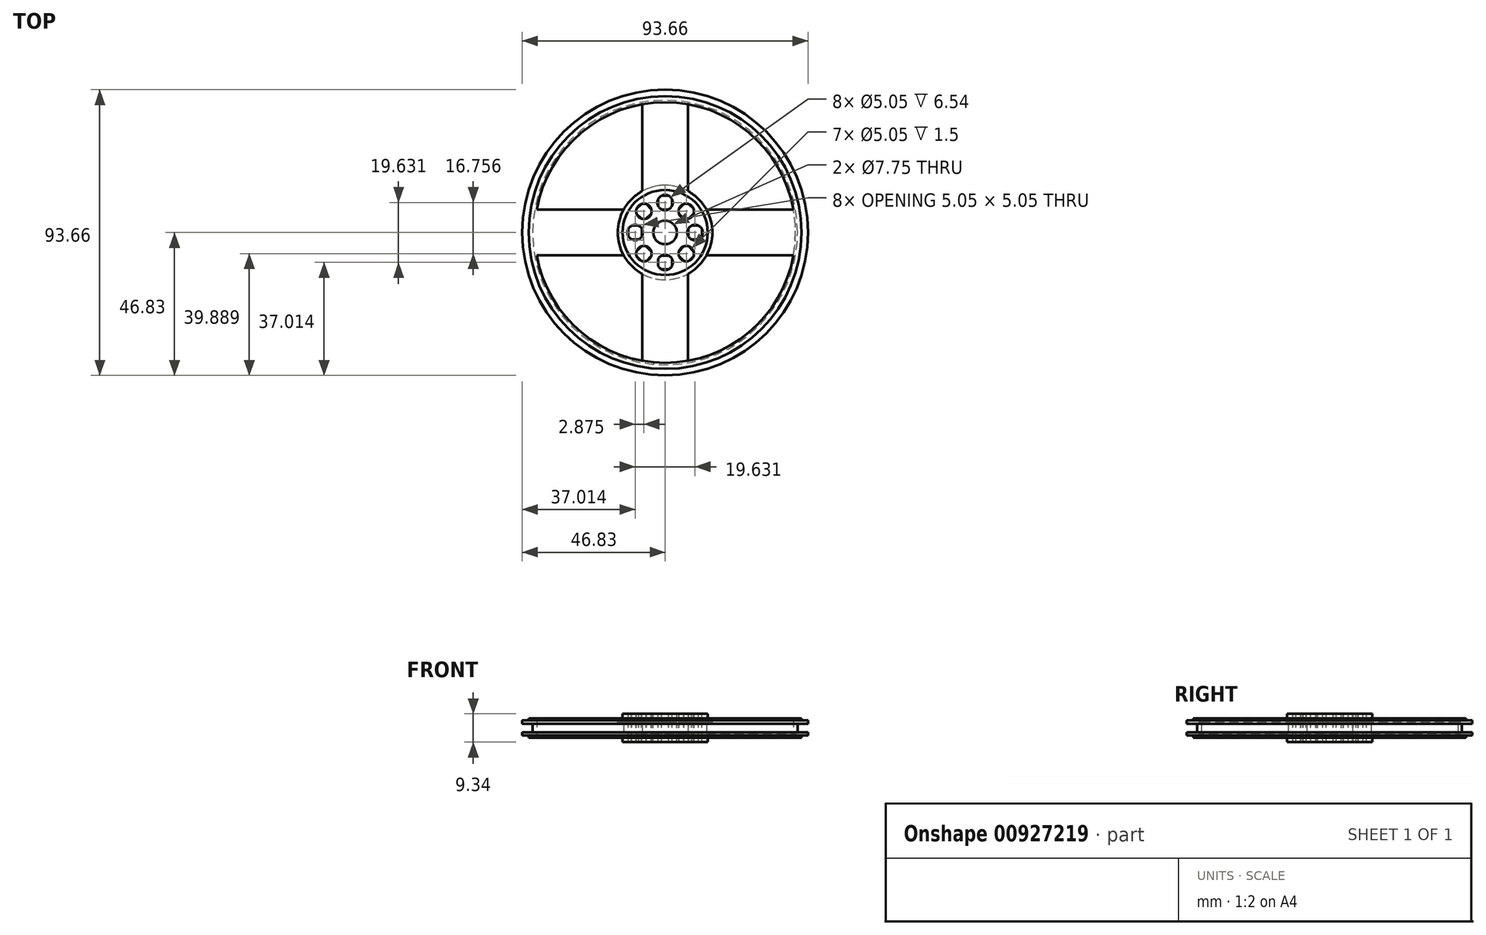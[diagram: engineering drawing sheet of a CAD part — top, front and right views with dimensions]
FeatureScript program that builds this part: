
annotation { "Feature Type Name" : "Feature", "Feature Type Description" : "" }
export const myFeature = defineFeature(function(context is Context, id is Id, definition is map)
    precondition{}
    {
        {
            var Q0;
            Q0=qCreatedBy(makeId("Top.planeOp"),FACE);
            var sketch = newSketch(context, id + "F0", { "sketchPlane" : qUnion([Q0])});
            skCircle(sketch, "E0", {"center": v(0, 0) * mm, "radius": 43.4 * mm});
            skSolve(sketch);
        }
        {
            var Q0;
            Q0 = qSketchRegion(id + "F0", true);
            extrude(context, id + "F1", {"entities" : qUnion([Q0]), "depth" : 2.82 * mm, "offsetDistance" : 25 * mm});
        }
        {
            var Q0;
            Q0=makeQuery(id+"F1.opExtrude","CAP_FACE",FACE,{"disambiguationData":[OSD([sQuery(id+"F0.wireOp",EDGE,"E0")])],"isStart":false});
            var sketch = newSketch(context, id + "F2", { "sketchPlane" : qUnion([Q0])});
            skCircle(sketch, "E1", {"center": v(0, 0) * mm, "radius": 46.83 * mm});
            skSolve(sketch);
        }
        {
            var Q0;
            Q0 = qSketchRegion(id + "F2", true);
            extrude(context, id + "F3", {"entities" : qUnion([Q0]), "operationType" : NewBodyOperationType.ADD, "depth" : 1.06 * mm, "offsetDistance" : 25 * mm});
        }
        {
            var Q0;
            Q0=makeQuery(id+"F1.opExtrude","CAP_FACE",FACE,{"disambiguationData":[OSD([sQuery(id+"F0.wireOp",EDGE,"E0")])],"isStart":true});
            var sketch = newSketch(context, id + "F4", { "sketchPlane" : qUnion([Q0])});
            skCircle(sketch, "E2.0", {"center": v(0, 0) * mm, "radius": 46.83 * mm});
            skSolve(sketch);
        }
        {
            var Q0;
            Q0 = qSketchRegion(id + "F4", true);
            extrude(context, id + "F5", {"entities" : qUnion([Q0]), "operationType" : NewBodyOperationType.ADD, "depth" : 1.06 * mm, "offsetDistance" : 25 * mm});
        }
        {
            var Q0;
            Q0=makeQuery(id+"F5.opExtrude","CAP_FACE",FACE,{"disambiguationData":[OSD([sQuery(id+"F4.wireOp",EDGE,"E2.0")])],"isStart":false});
            var sketch = newSketch(context, id + "F6", { "sketchPlane" : qUnion([Q0])});
            skCircle(sketch, "E3", {"center": v(0, 0) * mm, "radius": 44.73 * mm});
            skSolve(sketch);
        }
        {
            var Q0;
            Q0 = qSketchRegion(id + "F6", true);
            extrude(context, id + "F7", {"entities" : qUnion([Q0]), "operationType" : NewBodyOperationType.ADD, "depth" : .7 * mm, "offsetDistance" : 25 * mm});
        }
        {
            var Q0;
            Q0=makeQuery(id+"F3.opExtrude","CAP_FACE",FACE,{"disambiguationData":[OSD([sQuery(id+"F2.wireOp",EDGE,"E1")])],"isStart":false});
            var sketch = newSketch(context, id + "F8", { "sketchPlane" : qUnion([Q0])});
            skCircle(sketch, "E4.0", {"center": v(0, 0) * mm, "radius": 44.73 * mm});
            skSolve(sketch);
        }
        {
            var Q0;
            Q0 = qSketchRegion(id + "F8", true);
            extrude(context, id + "F9", {"entities" : qUnion([Q0]), "operationType" : NewBodyOperationType.ADD, "depth" : .7 * mm, "offsetDistance" : 25 * mm});
        }
        {
            var Q0;
            Q0=makeQuery(id+"F7.opExtrude","CAP_FACE",FACE,{"disambiguationData":[OSD([sQuery(id+"F6.wireOp",EDGE,"E3")])],"isStart":false});
            var sketch = newSketch(context, id + "F10", { "sketchPlane" : qUnion([Q0])});
            skCircle(sketch, "E5", {"center": v(0, 0) * mm, "radius": 15.5 * mm});
            skLineSegment(sketch, "E6", {"start": v(0, 0) * mm, "end": v(0, -44.73) * mm, "construction": true});
            skLineSegment(sketch, "E7", {"start": v(0, -44.73) * mm, "end": v(0, 44.73) * mm, "construction": true});
            skLineSegment(sketch, "E8", {"start": v(-44.73, 0) * mm, "end": v(44.73, 0) * mm, "construction": true});
            skLineSegment(sketch, "E9", {"start": v(-7.47, -13.58) * mm, "end": v(-7.47, -44.1) * mm});
            skLineSegment(sketch, "E10", {"start": v(7.47, -13.58) * mm, "end": v(7.47, -44.1) * mm});
            skLineSegment(sketch, "E11", {"start": v(7.47, -28.84) * mm, "end": v(0, -28.84) * mm, "construction": true});
            skLineSegment(sketch, "E12", {"start": v(0, -28.84) * mm, "end": v(-7.47, -28.84) * mm, "construction": true});
            skLineSegment(sketch, "E13.1.0", {"start": v(13.58, -7.48) * mm, "end": v(44.1, -7.48) * mm});
            skLineSegment(sketch, "E13.1.1", {"start": v(13.58, 7.47) * mm, "end": v(44.1, 7.47) * mm});
            skLineSegment(sketch, "E13.2.0", {"start": v(7.48, 13.58) * mm, "end": v(7.48, 44.1) * mm});
            skLineSegment(sketch, "E13.2.1", {"start": v(-7.47, 13.58) * mm, "end": v(-7.47, 44.1) * mm});
            skLineSegment(sketch, "E13.3.0", {"start": v(-13.58, 7.48) * mm, "end": v(-44.1, 7.48) * mm});
            skLineSegment(sketch, "E13.3.1", {"start": v(-13.58, -7.47) * mm, "end": v(-44.1, -7.47) * mm});
            skCircle(sketch, "E14", {"center": v(0, 0) * mm, "radius": 42.73 * mm});
            skSolve(sketch);
        }
        {
            var Q0;
            {var subQ0=sQuery(id+"F10.wireOp",EDGE,"E9");var subQ1=sQuery(id+"F10.wireOp",EDGE,"E5");var subQ2=makeQuery(id+"F10.imprint","INTERSECT",VERTEX,{"derivedFrom":[subQ1,subQ0]});Q0=makeQuery(id+"F10.imprint","IMPRINT",FACE,{"disambiguationData":[TD([[makeQuery(id+"F10.imprint","IMPRINT",EDGE,{"disambiguationData":[TD([[subQ2,1.0]])],"derivedFrom":subQ1}),-1.0]])]});}
            var Q1;
            {var subQ0=sQuery(id+"F10.wireOp",EDGE,"E13.2.1");var subQ1=sQuery(id+"F10.wireOp",EDGE,"E5");var subQ2=makeQuery(id+"F10.imprint","INTERSECT",VERTEX,{"derivedFrom":[subQ1,subQ0]});Q1=makeQuery(id+"F10.imprint","IMPRINT",FACE,{"disambiguationData":[TD([[makeQuery(id+"F10.imprint","IMPRINT",EDGE,{"disambiguationData":[TD([[subQ2,-1.0]])],"derivedFrom":subQ1}),-1.0]])]});}
            var Q2;
            {var subQ0=sQuery(id+"F10.wireOp",EDGE,"E13.1.1");var subQ1=sQuery(id+"F10.wireOp",EDGE,"E5");var subQ2=makeQuery(id+"F10.imprint","INTERSECT",VERTEX,{"derivedFrom":[subQ1,subQ0]});Q2=makeQuery(id+"F10.imprint","IMPRINT",FACE,{"disambiguationData":[TD([[makeQuery(id+"F10.imprint","IMPRINT",EDGE,{"disambiguationData":[TD([[subQ2,-1.0]])],"derivedFrom":subQ1}),-1.0]])]});}
            var Q3;
            {var subQ0=sQuery(id+"F10.wireOp",EDGE,"E10");var subQ1=sQuery(id+"F10.wireOp",EDGE,"E5");var subQ2=makeQuery(id+"F10.imprint","INTERSECT",VERTEX,{"derivedFrom":[subQ1,subQ0]});Q3=makeQuery(id+"F10.imprint","IMPRINT",FACE,{"disambiguationData":[TD([[makeQuery(id+"F10.imprint","IMPRINT",EDGE,{"disambiguationData":[TD([[subQ2,-1.0]])],"derivedFrom":subQ1}),-1.0]])]});}
            extrude(context, id + "F11", {"entities" : qUnion([Q0, Q1, Q2, Q3]), "operationType" : NewBodyOperationType.REMOVE, "oppositeDirection" : true, "depth" : 25 * mm, "offsetDistance" : 25 * mm});
        }
        {
            var Q0;
            {var subQ0=sQuery(id+"F10.wireOp",EDGE,"E13.3.0");Q0=makeQuery(id+"F10.imprint","IMPRINT",FACE,{"disambiguationData":[TD([[makeQuery(id+"F10.imprint","IMPRINT",EDGE,{"derivedFrom":subQ0}),1.0]])]});}
            var sketch = newSketch(context, id + "F12", { "sketchPlane" : qUnion([Q0])});
            skSolve(sketch);
        }
        {
            var Q0;
            {var subQ0=sQuery(id+"F10.wireOp",EDGE,"E13.3.0");var subQ1=sQuery(id+"F10.wireOp",EDGE,"E5");var subQ2=makeQuery(id+"F10.imprint","INTERSECT",VERTEX,{"derivedFrom":[subQ1,subQ0]});Q0=makeQuery(id+"F12.imprint","IMPRINT",FACE,{"disambiguationData":[TD([[makeQuery(id+"F12.imprint","IMPRINT",EDGE,{"derivedFrom":makeQuery(id+"F10.imprint","IMPRINT",EDGE,{"disambiguationData":[TD([[subQ2,-1.0]])],"derivedFrom":subQ1})}),-1.0]])]});}
            var Q1;
            {var subQ0=sQuery(id+"F10.wireOp",EDGE,"E9");var subQ1=sQuery(id+"F10.wireOp",EDGE,"E5");var subQ2=makeQuery(id+"F10.imprint","INTERSECT",VERTEX,{"derivedFrom":[subQ1,subQ0]});Q1=makeQuery(id+"F10.imprint","IMPRINT",FACE,{"disambiguationData":[TD([[makeQuery(id+"F10.imprint","IMPRINT",EDGE,{"disambiguationData":[TD([[subQ2,-1.0]])],"derivedFrom":subQ1}),-1.0]])]});}
            var Q2;
            {var subQ0=sQuery(id+"F10.wireOp",EDGE,"E13.1.0");var subQ1=sQuery(id+"F10.wireOp",EDGE,"E5");var subQ2=makeQuery(id+"F10.imprint","INTERSECT",VERTEX,{"derivedFrom":[subQ1,subQ0]});Q2=makeQuery(id+"F10.imprint","IMPRINT",FACE,{"disambiguationData":[TD([[makeQuery(id+"F10.imprint","IMPRINT",EDGE,{"disambiguationData":[TD([[subQ2,-1.0]])],"derivedFrom":subQ1}),-1.0]])]});}
            var Q3;
            {var subQ0=sQuery(id+"F10.wireOp",EDGE,"E13.2.0");var subQ1=sQuery(id+"F10.wireOp",EDGE,"E5");var subQ2=makeQuery(id+"F10.imprint","INTERSECT",VERTEX,{"derivedFrom":[subQ1,subQ0]});Q3=makeQuery(id+"F10.imprint","IMPRINT",FACE,{"disambiguationData":[TD([[makeQuery(id+"F10.imprint","IMPRINT",EDGE,{"disambiguationData":[TD([[subQ2,-1.0]])],"derivedFrom":subQ1}),-1.0]])]});}
            extrude(context, id + "F13", {"entities" : qUnion([Q0, Q1, Q2, Q3]), "operationType" : NewBodyOperationType.REMOVE, "oppositeDirection" : true, "depth" : 1.3 * mm, "offsetDistance" : 25 * mm});
        }
        {
            var Q0;
            Q0=makeQuery(id+"F9.opExtrude","CAP_FACE",FACE,{"disambiguationData":[OSD([sQuery(id+"F8.wireOp",EDGE,"E4.0")])],"isStart":false});
            var sketch = newSketch(context, id + "F14", { "sketchPlane" : qUnion([Q0])});
            skCircle(sketch, "E15.0", {"center": v(0, 0) * mm, "radius": 15.5 * mm});
            skLineSegment(sketch, "E16.0", {"start": v(-7.47, -13.58) * mm, "end": v(-7.47, -44.1) * mm});
            skCircle(sketch, "E17.0", {"center": v(0, 0) * mm, "radius": 42.73 * mm});
            skLineSegment(sketch, "E18.0", {"start": v(7.48, -42.07) * mm, "end": v(7.48, -13.58) * mm});
            skLineSegment(sketch, "E19.0", {"start": v(13.58, -7.47) * mm, "end": v(44.1, -7.47) * mm});
            skPoint(sketch, "E20.0", {"position": v(28.84, 7.48) * mm});
            skLineSegment(sketch, "E21.0", {"start": v(13.58, 7.48) * mm, "end": v(44.1, 7.48) * mm});
            skLineSegment(sketch, "E22.0", {"start": v(7.47, 42.07) * mm, "end": v(7.47, 13.58) * mm});
            skLineSegment(sketch, "E23.0", {"start": v(-7.47, 42.07) * mm, "end": v(-7.47, 13.58) * mm});
            skLineSegment(sketch, "E24.0", {"start": v(-13.58, 7.47) * mm, "end": v(-44.1, 7.47) * mm});
            skLineSegment(sketch, "E25.0", {"start": v(-13.58, -7.48) * mm, "end": v(-44.1, -7.48) * mm});
            skSolve(sketch);
        }
        {
            var Q0;
            {var subQ0=sQuery(id+"F14.wireOp",EDGE,"E18.0");Q0=makeQuery(id+"F14.imprint","IMPRINT",FACE,{"disambiguationData":[TD([[makeQuery(id+"F14.imprint","IMPRINT",EDGE,{"derivedFrom":subQ0}),1.0]])]});}
            var Q1;
            {var subQ0=sQuery(id+"F14.wireOp",EDGE,"E25.0");var subQ1=sQuery(id+"F14.wireOp",EDGE,"E15.0");var subQ2=makeQuery(id+"F14.imprint","INTERSECT",VERTEX,{"derivedFrom":[subQ1,subQ0]});var subQ3=sQuery(id+"F14.wireOp",EDGE,"E24.0");var subQ4=makeQuery(id+"F14.imprint","INTERSECT",VERTEX,{"derivedFrom":[subQ1,subQ3]});Q1=makeQuery(id+"F14.imprint","IMPRINT",FACE,{"disambiguationData":[TD([[makeQuery(id+"F14.imprint","IMPRINT",EDGE,{"disambiguationData":[TD([[subQ2,-1.0],[subQ4,1.0]])],"derivedFrom":subQ1}),1.0]])]});}
            var Q2;
            {var subQ2=sQuery(id+"F14.wireOp",EDGE,"E22.0");Q2=makeQuery(id+"F14.imprint","IMPRINT",FACE,{"disambiguationData":[TD([[makeQuery(id+"F14.imprint","IMPRINT",EDGE,{"derivedFrom":subQ2}),-1.0]])]});}
            var Q3;
            {var subQ0=sQuery(id+"F14.wireOp",EDGE,"E21.0");var subQ1=sQuery(id+"F14.wireOp",EDGE,"E15.0");var subQ2=makeQuery(id+"F14.imprint","INTERSECT",VERTEX,{"derivedFrom":[subQ1,subQ0]});var subQ3=sQuery(id+"F14.wireOp",EDGE,"E19.0");var subQ4=makeQuery(id+"F14.imprint","INTERSECT",VERTEX,{"derivedFrom":[subQ1,subQ3]});Q3=makeQuery(id+"F14.imprint","IMPRINT",FACE,{"disambiguationData":[TD([[makeQuery(id+"F14.imprint","IMPRINT",EDGE,{"disambiguationData":[TD([[subQ2,-1.0],[subQ4,1.0]])],"derivedFrom":subQ1}),1.0]])]});}
            extrude(context, id + "F15", {"entities" : qUnion([Q0, Q1, Q2, Q3]), "operationType" : NewBodyOperationType.REMOVE, "oppositeDirection" : true, "depth" : 1.3 * mm, "offsetDistance" : 25 * mm});
        }
        {
            var Q0;
            {var subQ0=sQuery(id+"F10.wireOp",EDGE,"E5");var subQ8=makeQuery(id+"F10.imprint","INTERSECT",VERTEX,{"derivedFrom":[subQ0,sQuery(id+"F10.wireOp",EDGE,"E13.1.1")]});Q0=makeQuery(id+"F13.boolean.opBoolean","SPLIT",FACE,{"disambiguationData":[TD([makeQuery(id+"F11.boolean.opBoolean","COPY",FACE,{"derivedFrom":makeQuery(id+"F11.opExtrude","SWEPT_FACE",FACE,{"disambiguationData":[OSD([subQ0]),TDD([makeQuery(id+"F10.imprint","IMPRINT",EDGE,{"disambiguationData":[TD([[subQ8,-1.0]])],"derivedFrom":subQ0})])]})})])],"derivedFrom":makeQuery(id+"F7.opExtrude","CAP_FACE",FACE,{"disambiguationData":[OSD([sQuery(id+"F6.wireOp",EDGE,"E3")])],"isStart":false})});}
            var sketch = newSketch(context, id + "F16", { "sketchPlane" : qUnion([Q0])});
            skCircle(sketch, "E26", {"center": v(0, 0) * mm, "radius": 13.95 * mm});
            skSolve(sketch);
        }
        {
            var Q0;
            Q0 = qSketchRegion(id + "F16", true);
            extrude(context, id + "F17", {"entities" : qUnion([Q0]), "operationType" : NewBodyOperationType.ADD, "depth" : 1.5 * mm, "offsetDistance" : 25 * mm});
        }
        {
            var Q0;
            {var subQ0=sQuery(id+"F10.wireOp",EDGE,"E5");Q0=makeQuery(id+"F15.boolean.opBoolean","SPLIT",FACE,{"disambiguationData":[TD([makeQuery(id+"F11.boolean.opBoolean","COPY",FACE,{"derivedFrom":makeQuery(id+"F11.opExtrude","SWEPT_FACE",FACE,{"disambiguationData":[OSD([subQ0]),TDD([makeQuery(id+"F10.imprint","IMPRINT",EDGE,{"disambiguationData":[TD([[makeQuery(id+"F10.imprint","INTERSECT",VERTEX,{"derivedFrom":[subQ0,sQuery(id+"F10.wireOp",EDGE,"E13.1.1")]}),-1.0]])],"derivedFrom":subQ0})])]})})])],"derivedFrom":makeQuery(id+"F9.opExtrude","CAP_FACE",FACE,{"disambiguationData":[OSD([sQuery(id+"F8.wireOp",EDGE,"E4.0")])],"isStart":false})});}
            var sketch = newSketch(context, id + "F18", { "sketchPlane" : qUnion([Q0])});
            skCircle(sketch, "E27.0", {"center": v(0, 0) * mm, "radius": 13.95 * mm});
            skSolve(sketch);
        }
        {
            var Q0;
            Q0 = qSketchRegion(id + "F18", true);
            extrude(context, id + "F19", {"entities" : qUnion([Q0]), "operationType" : NewBodyOperationType.ADD, "depth" : 1.5 * mm, "offsetDistance" : 25 * mm});
        }
        {
            var Q0;
            Q0=makeQuery(id+"F19.opExtrude","CAP_FACE",FACE,{"disambiguationData":[OSD([sQuery(id+"F18.wireOp",EDGE,"E27.0")])],"isStart":false});
            var sketch = newSketch(context, id + "F20", { "sketchPlane" : qUnion([Q0])});
            skCircle(sketch, "E28", {"center": v(0, 0) * mm, "radius": 3.88 * mm});
            skLineSegment(sketch, "E29", {"start": v(0, -13.95) * mm, "end": v(0, 13.95) * mm, "construction": true});
            skCircle(sketch, "E30", {"center": v(0, -9.82) * mm, "radius": 2.53 * mm});
            skCircle(sketch, "E31.1.0", {"center": v(6.94, -6.94) * mm, "radius": 2.53 * mm});
            skCircle(sketch, "E31.2.0", {"center": v(9.82, 0) * mm, "radius": 2.53 * mm});
            skCircle(sketch, "E31.3.0", {"center": v(6.94, 6.94) * mm, "radius": 2.53 * mm});
            skCircle(sketch, "E31.4.0", {"center": v(0, 9.82) * mm, "radius": 2.53 * mm});
            skCircle(sketch, "E31.5.0", {"center": v(-6.94, 6.94) * mm, "radius": 2.53 * mm});
            skCircle(sketch, "E31.6.0", {"center": v(-9.82, 0) * mm, "radius": 2.53 * mm});
            skCircle(sketch, "E31.7.0", {"center": v(-6.94, -6.94) * mm, "radius": 2.53 * mm});
            skSolve(sketch);
        }
        {
            var Q0;
            Q0 = qSketchRegion(id + "F20", true);
            extrude(context, id + "F21", {"entities" : qUnion([Q0]), "operationType" : NewBodyOperationType.REMOVE, "oppositeDirection" : true, "depth" : 25 * mm, "offsetDistance" : 25 * mm});
        }
        {
            var Q0;
            Q0=makeQuery(id+"F19.opExtrude","CAP_FACE",FACE,{"disambiguationData":[OSD([sQuery(id+"F18.wireOp",EDGE,"E27.0")])],"isStart":false});
            var sketch = newSketch(context, id + "F22", { "sketchPlane" : qUnion([Q0])});
            skLineSegment(sketch, "E32.bottom", {"start": v(2.25, -7.57) * mm, "end": v(-2.24, -7.57) * mm});
            skLineSegment(sketch, "E32.top", {"start": v(2.25, -12.06) * mm, "end": v(-2.24, -12.06) * mm});
            skLineSegment(sketch, "E32.left", {"start": v(2.25, -12.06) * mm, "end": v(2.25, -7.57) * mm});
            skLineSegment(sketch, "E32.right", {"start": v(-2.24, -12.06) * mm, "end": v(-2.24, -7.57) * mm});
            skLineSegment(sketch, "E33", {"start": v(0, -12.06) * mm, "end": v(0, -7.57) * mm, "construction": true});
            skPoint(sketch, "E34", {"position": v(0, -9.82) * mm});
            skCircle(sketch, "E35.0", {"center": v(0, -9.82) * mm, "radius": 2.53 * mm});
            skLineSegment(sketch, "E36.1.0", {"start": v(6.95, -3.76) * mm, "end": v(3.77, -6.94) * mm});
            skLineSegment(sketch, "E36.1.1", {"start": v(6.95, -10.11) * mm, "end": v(3.77, -6.94) * mm});
            skLineSegment(sketch, "E36.1.2", {"start": v(10.12, -6.94) * mm, "end": v(6.95, -10.11) * mm});
            skLineSegment(sketch, "E36.1.3", {"start": v(10.12, -6.94) * mm, "end": v(6.95, -3.76) * mm});
            skCircle(sketch, "E36.1.4", {"center": v(6.94, -6.94) * mm, "radius": 2.53 * mm});
            skLineSegment(sketch, "E36.2.0", {"start": v(7.57, 2.25) * mm, "end": v(7.57, -2.24) * mm});
            skLineSegment(sketch, "E36.2.1", {"start": v(12.06, -2.24) * mm, "end": v(7.57, -2.24) * mm});
            skLineSegment(sketch, "E36.2.2", {"start": v(12.06, 2.25) * mm, "end": v(12.06, -2.24) * mm});
            skLineSegment(sketch, "E36.2.3", {"start": v(12.06, 2.25) * mm, "end": v(7.57, 2.25) * mm});
            skCircle(sketch, "E36.2.4", {"center": v(9.82, 0) * mm, "radius": 2.53 * mm});
            skLineSegment(sketch, "E36.3.0", {"start": v(3.76, 6.95) * mm, "end": v(6.94, 3.77) * mm});
            skLineSegment(sketch, "E36.3.1", {"start": v(10.11, 6.95) * mm, "end": v(6.94, 3.77) * mm});
            skLineSegment(sketch, "E36.3.2", {"start": v(6.94, 10.12) * mm, "end": v(10.11, 6.95) * mm});
            skLineSegment(sketch, "E36.3.3", {"start": v(6.94, 10.12) * mm, "end": v(3.76, 6.95) * mm});
            skCircle(sketch, "E36.3.4", {"center": v(6.94, 6.94) * mm, "radius": 2.53 * mm});
            skLineSegment(sketch, "E36.4.0", {"start": v(-2.25, 7.57) * mm, "end": v(2.24, 7.57) * mm});
            skLineSegment(sketch, "E36.4.1", {"start": v(2.24, 12.06) * mm, "end": v(2.24, 7.57) * mm});
            skLineSegment(sketch, "E36.4.2", {"start": v(-2.25, 12.06) * mm, "end": v(2.24, 12.06) * mm});
            skLineSegment(sketch, "E36.4.3", {"start": v(-2.25, 12.06) * mm, "end": v(-2.25, 7.57) * mm});
            skCircle(sketch, "E36.4.4", {"center": v(0, 9.82) * mm, "radius": 2.53 * mm});
            skLineSegment(sketch, "E36.5.0", {"start": v(-6.95, 3.76) * mm, "end": v(-3.77, 6.94) * mm});
            skLineSegment(sketch, "E36.5.1", {"start": v(-6.95, 10.11) * mm, "end": v(-3.77, 6.94) * mm});
            skLineSegment(sketch, "E36.5.2", {"start": v(-10.12, 6.94) * mm, "end": v(-6.95, 10.11) * mm});
            skLineSegment(sketch, "E36.5.3", {"start": v(-10.12, 6.94) * mm, "end": v(-6.95, 3.76) * mm});
            skCircle(sketch, "E36.5.4", {"center": v(-6.94, 6.94) * mm, "radius": 2.53 * mm});
            skLineSegment(sketch, "E36.6.0", {"start": v(-7.57, -2.25) * mm, "end": v(-7.57, 2.24) * mm});
            skLineSegment(sketch, "E36.6.1", {"start": v(-12.06, 2.24) * mm, "end": v(-7.57, 2.24) * mm});
            skLineSegment(sketch, "E36.6.2", {"start": v(-12.06, -2.25) * mm, "end": v(-12.06, 2.24) * mm});
            skLineSegment(sketch, "E36.6.3", {"start": v(-12.06, -2.25) * mm, "end": v(-7.57, -2.25) * mm});
            skCircle(sketch, "E36.6.4", {"center": v(-9.82, 0) * mm, "radius": 2.53 * mm});
            skLineSegment(sketch, "E36.7.0", {"start": v(-3.76, -6.95) * mm, "end": v(-6.94, -3.77) * mm});
            skLineSegment(sketch, "E36.7.1", {"start": v(-10.11, -6.95) * mm, "end": v(-6.94, -3.77) * mm});
            skLineSegment(sketch, "E36.7.2", {"start": v(-6.94, -10.12) * mm, "end": v(-10.11, -6.95) * mm});
            skLineSegment(sketch, "E36.7.3", {"start": v(-6.94, -10.12) * mm, "end": v(-3.76, -6.95) * mm});
            skCircle(sketch, "E36.7.4", {"center": v(-6.94, -6.94) * mm, "radius": 2.53 * mm});
            skPoint(sketch, "E36.center", {"position": v(0, 0) * mm});
            skSolve(sketch);
        }
        {
            var Q0;
            {var subQ0=sQuery(id+"F22.wireOp",EDGE,"E36.1.4");var subQ1=sQuery(id+"F22.wireOp",EDGE,"E36.1.1");var subQ2=makeQuery(id+"F22.imprint","INTERSECT",VERTEX,{"disambiguationData":[OD(0.0)],"derivedFrom":[subQ1,subQ0]});Q0=makeQuery(id+"F22.imprint","IMPRINT",FACE,{"disambiguationData":[TD([[makeQuery(id+"F22.imprint","IMPRINT",EDGE,{"disambiguationData":[TD([[subQ2,-1.0]])],"derivedFrom":subQ1}),1.0]])]});}
            var Q1;
            {var subQ0=sQuery(id+"F22.wireOp",EDGE,"E36.1.4");var subQ1=sQuery(id+"F22.wireOp",EDGE,"E36.1.2");var subQ2=makeQuery(id+"F22.imprint","INTERSECT",VERTEX,{"disambiguationData":[OD(0.0)],"derivedFrom":[subQ1,subQ0]});Q1=makeQuery(id+"F22.imprint","IMPRINT",FACE,{"disambiguationData":[TD([[makeQuery(id+"F22.imprint","IMPRINT",EDGE,{"disambiguationData":[TD([[subQ2,-1.0]])],"derivedFrom":subQ1}),1.0]])]});}
            var Q2;
            {var subQ0=sQuery(id+"F22.wireOp",EDGE,"E36.1.4");var subQ1=sQuery(id+"F22.wireOp",EDGE,"E36.1.3");var subQ2=makeQuery(id+"F22.imprint","INTERSECT",VERTEX,{"disambiguationData":[OD(0.0)],"derivedFrom":[subQ1,subQ0]});Q2=makeQuery(id+"F22.imprint","IMPRINT",FACE,{"disambiguationData":[TD([[makeQuery(id+"F22.imprint","IMPRINT",EDGE,{"disambiguationData":[TD([[subQ2,-1.0]])],"derivedFrom":subQ1}),-1.0]])]});}
            var Q3;
            {var subQ0=sQuery(id+"F22.wireOp",EDGE,"E36.1.4");var subQ1=sQuery(id+"F22.wireOp",EDGE,"E36.1.0");var subQ2=makeQuery(id+"F22.imprint","INTERSECT",VERTEX,{"disambiguationData":[OD(0.0)],"derivedFrom":[subQ1,subQ0]});Q3=makeQuery(id+"F22.imprint","IMPRINT",FACE,{"disambiguationData":[TD([[makeQuery(id+"F22.imprint","IMPRINT",EDGE,{"disambiguationData":[TD([[subQ2,-1.0]])],"derivedFrom":subQ1}),-1.0]])]});}
            var Q4;
            {var subQ0=sQuery(id+"F22.wireOp",EDGE,"E35.0");var subQ1=sQuery(id+"F22.wireOp",EDGE,"E32.bottom");var subQ2=makeQuery(id+"F22.imprint","INTERSECT",VERTEX,{"disambiguationData":[OD(0.0)],"derivedFrom":[subQ1,subQ0]});Q4=makeQuery(id+"F22.imprint","IMPRINT",FACE,{"disambiguationData":[TD([[makeQuery(id+"F22.imprint","IMPRINT",EDGE,{"disambiguationData":[TD([[subQ2,-1.0]])],"derivedFrom":subQ1}),-1.0]])]});}
            var Q5;
            {var subQ0=sQuery(id+"F22.wireOp",EDGE,"E35.0");var subQ1=sQuery(id+"F22.wireOp",EDGE,"E32.left");var subQ2=makeQuery(id+"F22.imprint","INTERSECT",VERTEX,{"disambiguationData":[OD(0.0)],"derivedFrom":[subQ1,subQ0]});Q5=makeQuery(id+"F22.imprint","IMPRINT",FACE,{"disambiguationData":[TD([[makeQuery(id+"F22.imprint","IMPRINT",EDGE,{"disambiguationData":[TD([[subQ2,-1.0]])],"derivedFrom":subQ1}),-1.0]])]});}
            var Q6;
            {var subQ0=sQuery(id+"F22.wireOp",EDGE,"E35.0");var subQ1=sQuery(id+"F22.wireOp",EDGE,"E32.top");var subQ2=makeQuery(id+"F22.imprint","INTERSECT",VERTEX,{"disambiguationData":[OD(0.0)],"derivedFrom":[subQ1,subQ0]});Q6=makeQuery(id+"F22.imprint","IMPRINT",FACE,{"disambiguationData":[TD([[makeQuery(id+"F22.imprint","IMPRINT",EDGE,{"disambiguationData":[TD([[subQ2,-1.0]])],"derivedFrom":subQ1}),1.0]])]});}
            var Q7;
            {var subQ0=sQuery(id+"F22.wireOp",EDGE,"E35.0");var subQ1=sQuery(id+"F22.wireOp",EDGE,"E32.right");var subQ2=makeQuery(id+"F22.imprint","INTERSECT",VERTEX,{"disambiguationData":[OD(0.0)],"derivedFrom":[subQ1,subQ0]});Q7=makeQuery(id+"F22.imprint","IMPRINT",FACE,{"disambiguationData":[TD([[makeQuery(id+"F22.imprint","IMPRINT",EDGE,{"disambiguationData":[TD([[subQ2,-1.0]])],"derivedFrom":subQ1}),1.0]])]});}
            var Q8;
            {var subQ0=sQuery(id+"F22.wireOp",EDGE,"E36.7.4");var subQ1=sQuery(id+"F22.wireOp",EDGE,"E36.7.1");var subQ2=makeQuery(id+"F22.imprint","INTERSECT",VERTEX,{"disambiguationData":[OD(0.0)],"derivedFrom":[subQ1,subQ0]});Q8=makeQuery(id+"F22.imprint","IMPRINT",FACE,{"disambiguationData":[TD([[makeQuery(id+"F22.imprint","IMPRINT",EDGE,{"disambiguationData":[TD([[subQ2,-1.0]])],"derivedFrom":subQ1}),1.0]])]});}
            var Q9;
            {var subQ0=sQuery(id+"F22.wireOp",EDGE,"E36.7.4");var subQ1=sQuery(id+"F22.wireOp",EDGE,"E36.7.2");var subQ2=makeQuery(id+"F22.imprint","INTERSECT",VERTEX,{"disambiguationData":[OD(0.0)],"derivedFrom":[subQ1,subQ0]});Q9=makeQuery(id+"F22.imprint","IMPRINT",FACE,{"disambiguationData":[TD([[makeQuery(id+"F22.imprint","IMPRINT",EDGE,{"disambiguationData":[TD([[subQ2,-1.0]])],"derivedFrom":subQ1}),1.0]])]});}
            var Q10;
            {var subQ0=sQuery(id+"F22.wireOp",EDGE,"E36.7.4");var subQ1=sQuery(id+"F22.wireOp",EDGE,"E36.7.0");var subQ2=makeQuery(id+"F22.imprint","INTERSECT",VERTEX,{"disambiguationData":[OD(0.0)],"derivedFrom":[subQ1,subQ0]});Q10=makeQuery(id+"F22.imprint","IMPRINT",FACE,{"disambiguationData":[TD([[makeQuery(id+"F22.imprint","IMPRINT",EDGE,{"disambiguationData":[TD([[subQ2,-1.0]])],"derivedFrom":subQ1}),-1.0]])]});}
            var Q11;
            {var subQ0=sQuery(id+"F22.wireOp",EDGE,"E36.7.4");var subQ1=sQuery(id+"F22.wireOp",EDGE,"E36.7.3");var subQ2=makeQuery(id+"F22.imprint","INTERSECT",VERTEX,{"disambiguationData":[OD(0.0)],"derivedFrom":[subQ1,subQ0]});Q11=makeQuery(id+"F22.imprint","IMPRINT",FACE,{"disambiguationData":[TD([[makeQuery(id+"F22.imprint","IMPRINT",EDGE,{"disambiguationData":[TD([[subQ2,-1.0]])],"derivedFrom":subQ1}),-1.0]])]});}
            var Q12;
            {var subQ0=sQuery(id+"F22.wireOp",EDGE,"E36.6.4");var subQ1=sQuery(id+"F22.wireOp",EDGE,"E36.6.3");var subQ2=makeQuery(id+"F22.imprint","INTERSECT",VERTEX,{"disambiguationData":[OD(0.0)],"derivedFrom":[subQ1,subQ0]});Q12=makeQuery(id+"F22.imprint","IMPRINT",FACE,{"disambiguationData":[TD([[makeQuery(id+"F22.imprint","IMPRINT",EDGE,{"disambiguationData":[TD([[subQ2,-1.0]])],"derivedFrom":subQ1}),-1.0]])]});}
            var Q13;
            {var subQ0=sQuery(id+"F22.wireOp",EDGE,"E36.6.4");var subQ1=sQuery(id+"F22.wireOp",EDGE,"E36.6.1");var subQ2=makeQuery(id+"F22.imprint","INTERSECT",VERTEX,{"disambiguationData":[OD(0.0)],"derivedFrom":[subQ1,subQ0]});Q13=makeQuery(id+"F22.imprint","IMPRINT",FACE,{"disambiguationData":[TD([[makeQuery(id+"F22.imprint","IMPRINT",EDGE,{"disambiguationData":[TD([[subQ2,-1.0]])],"derivedFrom":subQ1}),1.0]])]});}
            var Q14;
            {var subQ0=sQuery(id+"F22.wireOp",EDGE,"E36.6.4");var subQ1=sQuery(id+"F22.wireOp",EDGE,"E36.6.0");var subQ2=makeQuery(id+"F22.imprint","INTERSECT",VERTEX,{"disambiguationData":[OD(0.0)],"derivedFrom":[subQ1,subQ0]});Q14=makeQuery(id+"F22.imprint","IMPRINT",FACE,{"disambiguationData":[TD([[makeQuery(id+"F22.imprint","IMPRINT",EDGE,{"disambiguationData":[TD([[subQ2,-1.0]])],"derivedFrom":subQ1}),-1.0]])]});}
            var Q15;
            {var subQ0=sQuery(id+"F22.wireOp",EDGE,"E36.6.4");var subQ1=sQuery(id+"F22.wireOp",EDGE,"E36.6.2");var subQ2=makeQuery(id+"F22.imprint","INTERSECT",VERTEX,{"disambiguationData":[OD(0.0)],"derivedFrom":[subQ1,subQ0]});Q15=makeQuery(id+"F22.imprint","IMPRINT",FACE,{"disambiguationData":[TD([[makeQuery(id+"F22.imprint","IMPRINT",EDGE,{"disambiguationData":[TD([[subQ2,-1.0]])],"derivedFrom":subQ1}),1.0]])]});}
            var Q16;
            {var subQ0=sQuery(id+"F22.wireOp",EDGE,"E36.5.4");var subQ1=sQuery(id+"F22.wireOp",EDGE,"E36.5.2");var subQ2=makeQuery(id+"F22.imprint","INTERSECT",VERTEX,{"disambiguationData":[OD(0.0)],"derivedFrom":[subQ1,subQ0]});Q16=makeQuery(id+"F22.imprint","IMPRINT",FACE,{"disambiguationData":[TD([[makeQuery(id+"F22.imprint","IMPRINT",EDGE,{"disambiguationData":[TD([[subQ2,-1.0]])],"derivedFrom":subQ1}),1.0]])]});}
            var Q17;
            {var subQ0=sQuery(id+"F22.wireOp",EDGE,"E36.5.4");var subQ1=sQuery(id+"F22.wireOp",EDGE,"E36.5.1");var subQ2=makeQuery(id+"F22.imprint","INTERSECT",VERTEX,{"disambiguationData":[OD(0.0)],"derivedFrom":[subQ1,subQ0]});Q17=makeQuery(id+"F22.imprint","IMPRINT",FACE,{"disambiguationData":[TD([[makeQuery(id+"F22.imprint","IMPRINT",EDGE,{"disambiguationData":[TD([[subQ2,-1.0]])],"derivedFrom":subQ1}),1.0]])]});}
            var Q18;
            {var subQ0=sQuery(id+"F22.wireOp",EDGE,"E36.5.4");var subQ1=sQuery(id+"F22.wireOp",EDGE,"E36.5.0");var subQ2=makeQuery(id+"F22.imprint","INTERSECT",VERTEX,{"disambiguationData":[OD(0.0)],"derivedFrom":[subQ1,subQ0]});Q18=makeQuery(id+"F22.imprint","IMPRINT",FACE,{"disambiguationData":[TD([[makeQuery(id+"F22.imprint","IMPRINT",EDGE,{"disambiguationData":[TD([[subQ2,-1.0]])],"derivedFrom":subQ1}),-1.0]])]});}
            var Q19;
            {var subQ0=sQuery(id+"F22.wireOp",EDGE,"E36.5.4");var subQ1=sQuery(id+"F22.wireOp",EDGE,"E36.5.3");var subQ2=makeQuery(id+"F22.imprint","INTERSECT",VERTEX,{"disambiguationData":[OD(0.0)],"derivedFrom":[subQ1,subQ0]});Q19=makeQuery(id+"F22.imprint","IMPRINT",FACE,{"disambiguationData":[TD([[makeQuery(id+"F22.imprint","IMPRINT",EDGE,{"disambiguationData":[TD([[subQ2,-1.0]])],"derivedFrom":subQ1}),-1.0]])]});}
            var Q20;
            {var subQ0=sQuery(id+"F22.wireOp",EDGE,"E36.4.4");var subQ1=sQuery(id+"F22.wireOp",EDGE,"E36.4.2");var subQ2=makeQuery(id+"F22.imprint","INTERSECT",VERTEX,{"disambiguationData":[OD(0.0)],"derivedFrom":[subQ1,subQ0]});Q20=makeQuery(id+"F22.imprint","IMPRINT",FACE,{"disambiguationData":[TD([[makeQuery(id+"F22.imprint","IMPRINT",EDGE,{"disambiguationData":[TD([[subQ2,-1.0]])],"derivedFrom":subQ1}),1.0]])]});}
            var Q21;
            {var subQ0=sQuery(id+"F22.wireOp",EDGE,"E36.4.4");var subQ1=sQuery(id+"F22.wireOp",EDGE,"E36.4.1");var subQ2=makeQuery(id+"F22.imprint","INTERSECT",VERTEX,{"disambiguationData":[OD(0.0)],"derivedFrom":[subQ1,subQ0]});Q21=makeQuery(id+"F22.imprint","IMPRINT",FACE,{"disambiguationData":[TD([[makeQuery(id+"F22.imprint","IMPRINT",EDGE,{"disambiguationData":[TD([[subQ2,-1.0]])],"derivedFrom":subQ1}),1.0]])]});}
            var Q22;
            {var subQ0=sQuery(id+"F22.wireOp",EDGE,"E36.4.4");var subQ1=sQuery(id+"F22.wireOp",EDGE,"E36.4.3");var subQ2=makeQuery(id+"F22.imprint","INTERSECT",VERTEX,{"disambiguationData":[OD(0.0)],"derivedFrom":[subQ1,subQ0]});Q22=makeQuery(id+"F22.imprint","IMPRINT",FACE,{"disambiguationData":[TD([[makeQuery(id+"F22.imprint","IMPRINT",EDGE,{"disambiguationData":[TD([[subQ2,-1.0]])],"derivedFrom":subQ1}),-1.0]])]});}
            var Q23;
            {var subQ0=sQuery(id+"F22.wireOp",EDGE,"E36.4.4");var subQ1=sQuery(id+"F22.wireOp",EDGE,"E36.4.0");var subQ2=makeQuery(id+"F22.imprint","INTERSECT",VERTEX,{"disambiguationData":[OD(0.0)],"derivedFrom":[subQ1,subQ0]});Q23=makeQuery(id+"F22.imprint","IMPRINT",FACE,{"disambiguationData":[TD([[makeQuery(id+"F22.imprint","IMPRINT",EDGE,{"disambiguationData":[TD([[subQ2,-1.0]])],"derivedFrom":subQ1}),-1.0]])]});}
            var Q24;
            {var subQ0=sQuery(id+"F22.wireOp",EDGE,"E36.3.4");var subQ1=sQuery(id+"F22.wireOp",EDGE,"E36.3.3");var subQ2=makeQuery(id+"F22.imprint","INTERSECT",VERTEX,{"disambiguationData":[OD(0.0)],"derivedFrom":[subQ1,subQ0]});Q24=makeQuery(id+"F22.imprint","IMPRINT",FACE,{"disambiguationData":[TD([[makeQuery(id+"F22.imprint","IMPRINT",EDGE,{"disambiguationData":[TD([[subQ2,-1.0]])],"derivedFrom":subQ1}),-1.0]])]});}
            var Q25;
            {var subQ0=sQuery(id+"F22.wireOp",EDGE,"E36.3.4");var subQ1=sQuery(id+"F22.wireOp",EDGE,"E36.3.2");var subQ2=makeQuery(id+"F22.imprint","INTERSECT",VERTEX,{"disambiguationData":[OD(0.0)],"derivedFrom":[subQ1,subQ0]});Q25=makeQuery(id+"F22.imprint","IMPRINT",FACE,{"disambiguationData":[TD([[makeQuery(id+"F22.imprint","IMPRINT",EDGE,{"disambiguationData":[TD([[subQ2,-1.0]])],"derivedFrom":subQ1}),1.0]])]});}
            var Q26;
            {var subQ0=sQuery(id+"F22.wireOp",EDGE,"E36.3.4");var subQ1=sQuery(id+"F22.wireOp",EDGE,"E36.3.0");var subQ2=makeQuery(id+"F22.imprint","INTERSECT",VERTEX,{"disambiguationData":[OD(0.0)],"derivedFrom":[subQ1,subQ0]});Q26=makeQuery(id+"F22.imprint","IMPRINT",FACE,{"disambiguationData":[TD([[makeQuery(id+"F22.imprint","IMPRINT",EDGE,{"disambiguationData":[TD([[subQ2,-1.0]])],"derivedFrom":subQ1}),-1.0]])]});}
            var Q27;
            {var subQ0=sQuery(id+"F22.wireOp",EDGE,"E36.3.4");var subQ1=sQuery(id+"F22.wireOp",EDGE,"E36.3.1");var subQ2=makeQuery(id+"F22.imprint","INTERSECT",VERTEX,{"disambiguationData":[OD(0.0)],"derivedFrom":[subQ1,subQ0]});Q27=makeQuery(id+"F22.imprint","IMPRINT",FACE,{"disambiguationData":[TD([[makeQuery(id+"F22.imprint","IMPRINT",EDGE,{"disambiguationData":[TD([[subQ2,-1.0]])],"derivedFrom":subQ1}),1.0]])]});}
            var Q28;
            {var subQ0=sQuery(id+"F22.wireOp",EDGE,"E36.2.4");var subQ1=sQuery(id+"F22.wireOp",EDGE,"E36.2.3");var subQ2=makeQuery(id+"F22.imprint","INTERSECT",VERTEX,{"disambiguationData":[OD(0.0)],"derivedFrom":[subQ1,subQ0]});Q28=makeQuery(id+"F22.imprint","IMPRINT",FACE,{"disambiguationData":[TD([[makeQuery(id+"F22.imprint","IMPRINT",EDGE,{"disambiguationData":[TD([[subQ2,-1.0]])],"derivedFrom":subQ1}),-1.0]])]});}
            var Q29;
            {var subQ0=sQuery(id+"F22.wireOp",EDGE,"E36.2.4");var subQ1=sQuery(id+"F22.wireOp",EDGE,"E36.2.0");var subQ2=makeQuery(id+"F22.imprint","INTERSECT",VERTEX,{"disambiguationData":[OD(0.0)],"derivedFrom":[subQ1,subQ0]});Q29=makeQuery(id+"F22.imprint","IMPRINT",FACE,{"disambiguationData":[TD([[makeQuery(id+"F22.imprint","IMPRINT",EDGE,{"disambiguationData":[TD([[subQ2,-1.0]])],"derivedFrom":subQ1}),-1.0]])]});}
            var Q30;
            {var subQ0=sQuery(id+"F22.wireOp",EDGE,"E36.2.4");var subQ1=sQuery(id+"F22.wireOp",EDGE,"E36.2.2");var subQ2=makeQuery(id+"F22.imprint","INTERSECT",VERTEX,{"disambiguationData":[OD(0.0)],"derivedFrom":[subQ1,subQ0]});Q30=makeQuery(id+"F22.imprint","IMPRINT",FACE,{"disambiguationData":[TD([[makeQuery(id+"F22.imprint","IMPRINT",EDGE,{"disambiguationData":[TD([[subQ2,-1.0]])],"derivedFrom":subQ1}),1.0]])]});}
            var Q31;
            {var subQ0=sQuery(id+"F22.wireOp",EDGE,"E36.2.4");var subQ1=sQuery(id+"F22.wireOp",EDGE,"E36.2.1");var subQ2=makeQuery(id+"F22.imprint","INTERSECT",VERTEX,{"disambiguationData":[OD(0.0)],"derivedFrom":[subQ1,subQ0]});Q31=makeQuery(id+"F22.imprint","IMPRINT",FACE,{"disambiguationData":[TD([[makeQuery(id+"F22.imprint","IMPRINT",EDGE,{"disambiguationData":[TD([[subQ2,-1.0]])],"derivedFrom":subQ1}),1.0]])]});}
            extrude(context, id + "F23", {"entities" : qUnion([Q0, Q1, Q2, Q3, Q4, Q5, Q6, Q7, Q8, Q9, Q10, Q11, Q12, Q13, Q14, Q15, Q16, Q17, Q18, Q19, Q20, Q21, Q22, Q23, Q24, Q25, Q26, Q27, Q28, Q29, Q30, Q31]), "operationType" : NewBodyOperationType.ADD, "oppositeDirection" : true, "depth" : 9.2 * mm, "offsetDistance" : 25 * mm});
        }
        {
            var Q0;
            {var subQ0=sQuery(id+"F22.wireOp",EDGE,"E36.1.4");var subQ1=sQuery(id+"F22.wireOp",EDGE,"E36.1.3");var subQ2=makeQuery(id+"F22.imprint","INTERSECT",VERTEX,{"disambiguationData":[OD(0.0)],"derivedFrom":[subQ1,subQ0]});Q0=makeQuery(id+"F22.imprint","IMPRINT",FACE,{"disambiguationData":[TD([[makeQuery(id+"F22.imprint","IMPRINT",EDGE,{"disambiguationData":[TD([[subQ2,-1.0]])],"derivedFrom":subQ1}),-1.0]])]});}
            var Q1;
            {var subQ0=sQuery(id+"F22.wireOp",EDGE,"E36.1.4");var subQ1=sQuery(id+"F22.wireOp",EDGE,"E36.1.2");var subQ2=makeQuery(id+"F22.imprint","INTERSECT",VERTEX,{"disambiguationData":[OD(0.0)],"derivedFrom":[subQ1,subQ0]});Q1=makeQuery(id+"F22.imprint","IMPRINT",FACE,{"disambiguationData":[TD([[makeQuery(id+"F22.imprint","IMPRINT",EDGE,{"disambiguationData":[TD([[subQ2,-1.0]])],"derivedFrom":subQ1}),1.0]])]});}
            var Q2;
            {var subQ0=sQuery(id+"F22.wireOp",EDGE,"E36.1.4");var subQ1=sQuery(id+"F22.wireOp",EDGE,"E36.1.1");var subQ2=makeQuery(id+"F22.imprint","INTERSECT",VERTEX,{"disambiguationData":[OD(0.0)],"derivedFrom":[subQ1,subQ0]});Q2=makeQuery(id+"F22.imprint","IMPRINT",FACE,{"disambiguationData":[TD([[makeQuery(id+"F22.imprint","IMPRINT",EDGE,{"disambiguationData":[TD([[subQ2,-1.0]])],"derivedFrom":subQ1}),1.0]])]});}
            var Q3;
            {var subQ0=sQuery(id+"F22.wireOp",EDGE,"E36.1.4");var subQ1=sQuery(id+"F22.wireOp",EDGE,"E36.1.0");var subQ2=makeQuery(id+"F22.imprint","INTERSECT",VERTEX,{"disambiguationData":[OD(0.0)],"derivedFrom":[subQ1,subQ0]});Q3=makeQuery(id+"F22.imprint","IMPRINT",FACE,{"disambiguationData":[TD([[makeQuery(id+"F22.imprint","IMPRINT",EDGE,{"disambiguationData":[TD([[subQ2,-1.0]])],"derivedFrom":subQ1}),-1.0]])]});}
            var Q4;
            {var subQ0=sQuery(id+"F22.wireOp",EDGE,"E35.0");var subQ1=sQuery(id+"F22.wireOp",EDGE,"E32.bottom");var subQ2=makeQuery(id+"F22.imprint","INTERSECT",VERTEX,{"disambiguationData":[OD(0.0)],"derivedFrom":[subQ1,subQ0]});Q4=makeQuery(id+"F22.imprint","IMPRINT",FACE,{"disambiguationData":[TD([[makeQuery(id+"F22.imprint","IMPRINT",EDGE,{"disambiguationData":[TD([[subQ2,-1.0]])],"derivedFrom":subQ1}),-1.0]])]});}
            var Q5;
            {var subQ0=sQuery(id+"F22.wireOp",EDGE,"E35.0");var subQ1=sQuery(id+"F22.wireOp",EDGE,"E32.left");var subQ2=makeQuery(id+"F22.imprint","INTERSECT",VERTEX,{"disambiguationData":[OD(0.0)],"derivedFrom":[subQ1,subQ0]});Q5=makeQuery(id+"F22.imprint","IMPRINT",FACE,{"disambiguationData":[TD([[makeQuery(id+"F22.imprint","IMPRINT",EDGE,{"disambiguationData":[TD([[subQ2,-1.0]])],"derivedFrom":subQ1}),-1.0]])]});}
            var Q6;
            {var subQ0=sQuery(id+"F22.wireOp",EDGE,"E35.0");var subQ1=sQuery(id+"F22.wireOp",EDGE,"E32.top");var subQ2=makeQuery(id+"F22.imprint","INTERSECT",VERTEX,{"disambiguationData":[OD(0.0)],"derivedFrom":[subQ1,subQ0]});Q6=makeQuery(id+"F22.imprint","IMPRINT",FACE,{"disambiguationData":[TD([[makeQuery(id+"F22.imprint","IMPRINT",EDGE,{"disambiguationData":[TD([[subQ2,-1.0]])],"derivedFrom":subQ1}),1.0]])]});}
            var Q7;
            {var subQ0=sQuery(id+"F22.wireOp",EDGE,"E36.7.4");var subQ1=sQuery(id+"F22.wireOp",EDGE,"E36.7.0");var subQ2=makeQuery(id+"F22.imprint","INTERSECT",VERTEX,{"disambiguationData":[OD(0.0)],"derivedFrom":[subQ1,subQ0]});Q7=makeQuery(id+"F22.imprint","IMPRINT",FACE,{"disambiguationData":[TD([[makeQuery(id+"F22.imprint","IMPRINT",EDGE,{"disambiguationData":[TD([[subQ2,-1.0]])],"derivedFrom":subQ1}),-1.0]])]});}
            var Q8;
            {var subQ0=sQuery(id+"F22.wireOp",EDGE,"E36.7.4");var subQ1=sQuery(id+"F22.wireOp",EDGE,"E36.7.3");var subQ2=makeQuery(id+"F22.imprint","INTERSECT",VERTEX,{"disambiguationData":[OD(0.0)],"derivedFrom":[subQ1,subQ0]});Q8=makeQuery(id+"F22.imprint","IMPRINT",FACE,{"disambiguationData":[TD([[makeQuery(id+"F22.imprint","IMPRINT",EDGE,{"disambiguationData":[TD([[subQ2,-1.0]])],"derivedFrom":subQ1}),-1.0]])]});}
            var Q9;
            {var subQ0=sQuery(id+"F22.wireOp",EDGE,"E36.7.4");var subQ1=sQuery(id+"F22.wireOp",EDGE,"E36.7.2");var subQ2=makeQuery(id+"F22.imprint","INTERSECT",VERTEX,{"disambiguationData":[OD(0.0)],"derivedFrom":[subQ1,subQ0]});Q9=makeQuery(id+"F22.imprint","IMPRINT",FACE,{"disambiguationData":[TD([[makeQuery(id+"F22.imprint","IMPRINT",EDGE,{"disambiguationData":[TD([[subQ2,-1.0]])],"derivedFrom":subQ1}),1.0]])]});}
            var Q10;
            {var subQ0=sQuery(id+"F22.wireOp",EDGE,"E36.7.4");var subQ1=sQuery(id+"F22.wireOp",EDGE,"E36.7.1");var subQ2=makeQuery(id+"F22.imprint","INTERSECT",VERTEX,{"disambiguationData":[OD(0.0)],"derivedFrom":[subQ1,subQ0]});Q10=makeQuery(id+"F22.imprint","IMPRINT",FACE,{"disambiguationData":[TD([[makeQuery(id+"F22.imprint","IMPRINT",EDGE,{"disambiguationData":[TD([[subQ2,-1.0]])],"derivedFrom":subQ1}),1.0]])]});}
            var Q11;
            {var subQ0=sQuery(id+"F22.wireOp",EDGE,"E36.6.4");var subQ1=sQuery(id+"F22.wireOp",EDGE,"E36.6.1");var subQ2=makeQuery(id+"F22.imprint","INTERSECT",VERTEX,{"disambiguationData":[OD(0.0)],"derivedFrom":[subQ1,subQ0]});Q11=makeQuery(id+"F22.imprint","IMPRINT",FACE,{"disambiguationData":[TD([[makeQuery(id+"F22.imprint","IMPRINT",EDGE,{"disambiguationData":[TD([[subQ2,-1.0]])],"derivedFrom":subQ1}),1.0]])]});}
            var Q12;
            {var subQ0=sQuery(id+"F22.wireOp",EDGE,"E36.6.4");var subQ1=sQuery(id+"F22.wireOp",EDGE,"E36.6.0");var subQ2=makeQuery(id+"F22.imprint","INTERSECT",VERTEX,{"disambiguationData":[OD(0.0)],"derivedFrom":[subQ1,subQ0]});Q12=makeQuery(id+"F22.imprint","IMPRINT",FACE,{"disambiguationData":[TD([[makeQuery(id+"F22.imprint","IMPRINT",EDGE,{"disambiguationData":[TD([[subQ2,-1.0]])],"derivedFrom":subQ1}),-1.0]])]});}
            var Q13;
            {var subQ0=sQuery(id+"F22.wireOp",EDGE,"E36.6.4");var subQ1=sQuery(id+"F22.wireOp",EDGE,"E36.6.3");var subQ2=makeQuery(id+"F22.imprint","INTERSECT",VERTEX,{"disambiguationData":[OD(0.0)],"derivedFrom":[subQ1,subQ0]});Q13=makeQuery(id+"F22.imprint","IMPRINT",FACE,{"disambiguationData":[TD([[makeQuery(id+"F22.imprint","IMPRINT",EDGE,{"disambiguationData":[TD([[subQ2,-1.0]])],"derivedFrom":subQ1}),-1.0]])]});}
            var Q14;
            {var subQ0=sQuery(id+"F22.wireOp",EDGE,"E36.6.4");var subQ1=sQuery(id+"F22.wireOp",EDGE,"E36.6.2");var subQ2=makeQuery(id+"F22.imprint","INTERSECT",VERTEX,{"disambiguationData":[OD(0.0)],"derivedFrom":[subQ1,subQ0]});Q14=makeQuery(id+"F22.imprint","IMPRINT",FACE,{"disambiguationData":[TD([[makeQuery(id+"F22.imprint","IMPRINT",EDGE,{"disambiguationData":[TD([[subQ2,-1.0]])],"derivedFrom":subQ1}),1.0]])]});}
            var Q15;
            {var subQ0=sQuery(id+"F22.wireOp",EDGE,"E36.5.4");var subQ1=sQuery(id+"F22.wireOp",EDGE,"E36.5.0");var subQ2=makeQuery(id+"F22.imprint","INTERSECT",VERTEX,{"disambiguationData":[OD(0.0)],"derivedFrom":[subQ1,subQ0]});Q15=makeQuery(id+"F22.imprint","IMPRINT",FACE,{"disambiguationData":[TD([[makeQuery(id+"F22.imprint","IMPRINT",EDGE,{"disambiguationData":[TD([[subQ2,-1.0]])],"derivedFrom":subQ1}),-1.0]])]});}
            var Q16;
            {var subQ0=sQuery(id+"F22.wireOp",EDGE,"E36.5.4");var subQ1=sQuery(id+"F22.wireOp",EDGE,"E36.5.1");var subQ2=makeQuery(id+"F22.imprint","INTERSECT",VERTEX,{"disambiguationData":[OD(0.0)],"derivedFrom":[subQ1,subQ0]});Q16=makeQuery(id+"F22.imprint","IMPRINT",FACE,{"disambiguationData":[TD([[makeQuery(id+"F22.imprint","IMPRINT",EDGE,{"disambiguationData":[TD([[subQ2,-1.0]])],"derivedFrom":subQ1}),1.0]])]});}
            var Q17;
            {var subQ0=sQuery(id+"F22.wireOp",EDGE,"E36.5.4");var subQ1=sQuery(id+"F22.wireOp",EDGE,"E36.5.2");var subQ2=makeQuery(id+"F22.imprint","INTERSECT",VERTEX,{"disambiguationData":[OD(0.0)],"derivedFrom":[subQ1,subQ0]});Q17=makeQuery(id+"F22.imprint","IMPRINT",FACE,{"disambiguationData":[TD([[makeQuery(id+"F22.imprint","IMPRINT",EDGE,{"disambiguationData":[TD([[subQ2,-1.0]])],"derivedFrom":subQ1}),1.0]])]});}
            var Q18;
            {var subQ0=sQuery(id+"F22.wireOp",EDGE,"E36.5.4");var subQ1=sQuery(id+"F22.wireOp",EDGE,"E36.5.3");var subQ2=makeQuery(id+"F22.imprint","INTERSECT",VERTEX,{"disambiguationData":[OD(0.0)],"derivedFrom":[subQ1,subQ0]});Q18=makeQuery(id+"F22.imprint","IMPRINT",FACE,{"disambiguationData":[TD([[makeQuery(id+"F22.imprint","IMPRINT",EDGE,{"disambiguationData":[TD([[subQ2,-1.0]])],"derivedFrom":subQ1}),-1.0]])]});}
            var Q19;
            {var subQ0=sQuery(id+"F22.wireOp",EDGE,"E36.4.4");var subQ1=sQuery(id+"F22.wireOp",EDGE,"E36.4.0");var subQ2=makeQuery(id+"F22.imprint","INTERSECT",VERTEX,{"disambiguationData":[OD(0.0)],"derivedFrom":[subQ1,subQ0]});Q19=makeQuery(id+"F22.imprint","IMPRINT",FACE,{"disambiguationData":[TD([[makeQuery(id+"F22.imprint","IMPRINT",EDGE,{"disambiguationData":[TD([[subQ2,-1.0]])],"derivedFrom":subQ1}),-1.0]])]});}
            var Q20;
            {var subQ0=sQuery(id+"F22.wireOp",EDGE,"E36.4.4");var subQ1=sQuery(id+"F22.wireOp",EDGE,"E36.4.3");var subQ2=makeQuery(id+"F22.imprint","INTERSECT",VERTEX,{"disambiguationData":[OD(0.0)],"derivedFrom":[subQ1,subQ0]});Q20=makeQuery(id+"F22.imprint","IMPRINT",FACE,{"disambiguationData":[TD([[makeQuery(id+"F22.imprint","IMPRINT",EDGE,{"disambiguationData":[TD([[subQ2,-1.0]])],"derivedFrom":subQ1}),-1.0]])]});}
            var Q21;
            {var subQ0=sQuery(id+"F22.wireOp",EDGE,"E36.4.4");var subQ1=sQuery(id+"F22.wireOp",EDGE,"E36.4.2");var subQ2=makeQuery(id+"F22.imprint","INTERSECT",VERTEX,{"disambiguationData":[OD(0.0)],"derivedFrom":[subQ1,subQ0]});Q21=makeQuery(id+"F22.imprint","IMPRINT",FACE,{"disambiguationData":[TD([[makeQuery(id+"F22.imprint","IMPRINT",EDGE,{"disambiguationData":[TD([[subQ2,-1.0]])],"derivedFrom":subQ1}),1.0]])]});}
            var Q22;
            {var subQ0=sQuery(id+"F22.wireOp",EDGE,"E36.4.4");var subQ1=sQuery(id+"F22.wireOp",EDGE,"E36.4.1");var subQ2=makeQuery(id+"F22.imprint","INTERSECT",VERTEX,{"disambiguationData":[OD(0.0)],"derivedFrom":[subQ1,subQ0]});Q22=makeQuery(id+"F22.imprint","IMPRINT",FACE,{"disambiguationData":[TD([[makeQuery(id+"F22.imprint","IMPRINT",EDGE,{"disambiguationData":[TD([[subQ2,-1.0]])],"derivedFrom":subQ1}),1.0]])]});}
            var Q23;
            {var subQ0=sQuery(id+"F22.wireOp",EDGE,"E36.3.4");var subQ1=sQuery(id+"F22.wireOp",EDGE,"E36.3.2");var subQ2=makeQuery(id+"F22.imprint","INTERSECT",VERTEX,{"disambiguationData":[OD(0.0)],"derivedFrom":[subQ1,subQ0]});Q23=makeQuery(id+"F22.imprint","IMPRINT",FACE,{"disambiguationData":[TD([[makeQuery(id+"F22.imprint","IMPRINT",EDGE,{"disambiguationData":[TD([[subQ2,-1.0]])],"derivedFrom":subQ1}),1.0]])]});}
            var Q24;
            {var subQ0=sQuery(id+"F22.wireOp",EDGE,"E36.3.4");var subQ1=sQuery(id+"F22.wireOp",EDGE,"E36.3.1");var subQ2=makeQuery(id+"F22.imprint","INTERSECT",VERTEX,{"disambiguationData":[OD(0.0)],"derivedFrom":[subQ1,subQ0]});Q24=makeQuery(id+"F22.imprint","IMPRINT",FACE,{"disambiguationData":[TD([[makeQuery(id+"F22.imprint","IMPRINT",EDGE,{"disambiguationData":[TD([[subQ2,-1.0]])],"derivedFrom":subQ1}),1.0]])]});}
            var Q25;
            {var subQ0=sQuery(id+"F22.wireOp",EDGE,"E36.3.4");var subQ1=sQuery(id+"F22.wireOp",EDGE,"E36.3.3");var subQ2=makeQuery(id+"F22.imprint","INTERSECT",VERTEX,{"disambiguationData":[OD(0.0)],"derivedFrom":[subQ1,subQ0]});Q25=makeQuery(id+"F22.imprint","IMPRINT",FACE,{"disambiguationData":[TD([[makeQuery(id+"F22.imprint","IMPRINT",EDGE,{"disambiguationData":[TD([[subQ2,-1.0]])],"derivedFrom":subQ1}),-1.0]])]});}
            var Q26;
            {var subQ0=sQuery(id+"F22.wireOp",EDGE,"E36.3.4");var subQ1=sQuery(id+"F22.wireOp",EDGE,"E36.3.0");var subQ2=makeQuery(id+"F22.imprint","INTERSECT",VERTEX,{"disambiguationData":[OD(0.0)],"derivedFrom":[subQ1,subQ0]});Q26=makeQuery(id+"F22.imprint","IMPRINT",FACE,{"disambiguationData":[TD([[makeQuery(id+"F22.imprint","IMPRINT",EDGE,{"disambiguationData":[TD([[subQ2,-1.0]])],"derivedFrom":subQ1}),-1.0]])]});}
            var Q27;
            {var subQ0=sQuery(id+"F22.wireOp",EDGE,"E36.2.4");var subQ1=sQuery(id+"F22.wireOp",EDGE,"E36.2.3");var subQ2=makeQuery(id+"F22.imprint","INTERSECT",VERTEX,{"disambiguationData":[OD(0.0)],"derivedFrom":[subQ1,subQ0]});Q27=makeQuery(id+"F22.imprint","IMPRINT",FACE,{"disambiguationData":[TD([[makeQuery(id+"F22.imprint","IMPRINT",EDGE,{"disambiguationData":[TD([[subQ2,-1.0]])],"derivedFrom":subQ1}),-1.0]])]});}
            var Q28;
            {var subQ0=sQuery(id+"F22.wireOp",EDGE,"E36.2.4");var subQ1=sQuery(id+"F22.wireOp",EDGE,"E36.2.2");var subQ2=makeQuery(id+"F22.imprint","INTERSECT",VERTEX,{"disambiguationData":[OD(0.0)],"derivedFrom":[subQ1,subQ0]});Q28=makeQuery(id+"F22.imprint","IMPRINT",FACE,{"disambiguationData":[TD([[makeQuery(id+"F22.imprint","IMPRINT",EDGE,{"disambiguationData":[TD([[subQ2,-1.0]])],"derivedFrom":subQ1}),1.0]])]});}
            var Q29;
            {var subQ0=sQuery(id+"F22.wireOp",EDGE,"E36.2.4");var subQ1=sQuery(id+"F22.wireOp",EDGE,"E36.2.0");var subQ2=makeQuery(id+"F22.imprint","INTERSECT",VERTEX,{"disambiguationData":[OD(0.0)],"derivedFrom":[subQ1,subQ0]});Q29=makeQuery(id+"F22.imprint","IMPRINT",FACE,{"disambiguationData":[TD([[makeQuery(id+"F22.imprint","IMPRINT",EDGE,{"disambiguationData":[TD([[subQ2,-1.0]])],"derivedFrom":subQ1}),-1.0]])]});}
            var Q30;
            {var subQ0=sQuery(id+"F22.wireOp",EDGE,"E36.2.4");var subQ1=sQuery(id+"F22.wireOp",EDGE,"E36.2.1");var subQ2=makeQuery(id+"F22.imprint","INTERSECT",VERTEX,{"disambiguationData":[OD(0.0)],"derivedFrom":[subQ1,subQ0]});Q30=makeQuery(id+"F22.imprint","IMPRINT",FACE,{"disambiguationData":[TD([[makeQuery(id+"F22.imprint","IMPRINT",EDGE,{"disambiguationData":[TD([[subQ2,-1.0]])],"derivedFrom":subQ1}),1.0]])]});}
            extrude(context, id + "F24", {"entities" : qUnion([Q0, Q1, Q2, Q3, Q4, Q5, Q6, Q7, Q8, Q9, Q10, Q11, Q12, Q13, Q14, Q15, Q16, Q17, Q18, Q19, Q20, Q21, Q22, Q23, Q24, Q25, Q26, Q27, Q28, Q29, Q30]), "operationType" : NewBodyOperationType.REMOVE, "oppositeDirection" : true, "depth" : 0.15 * mm, "offsetDistance" : 25 * mm});
        }
    });
